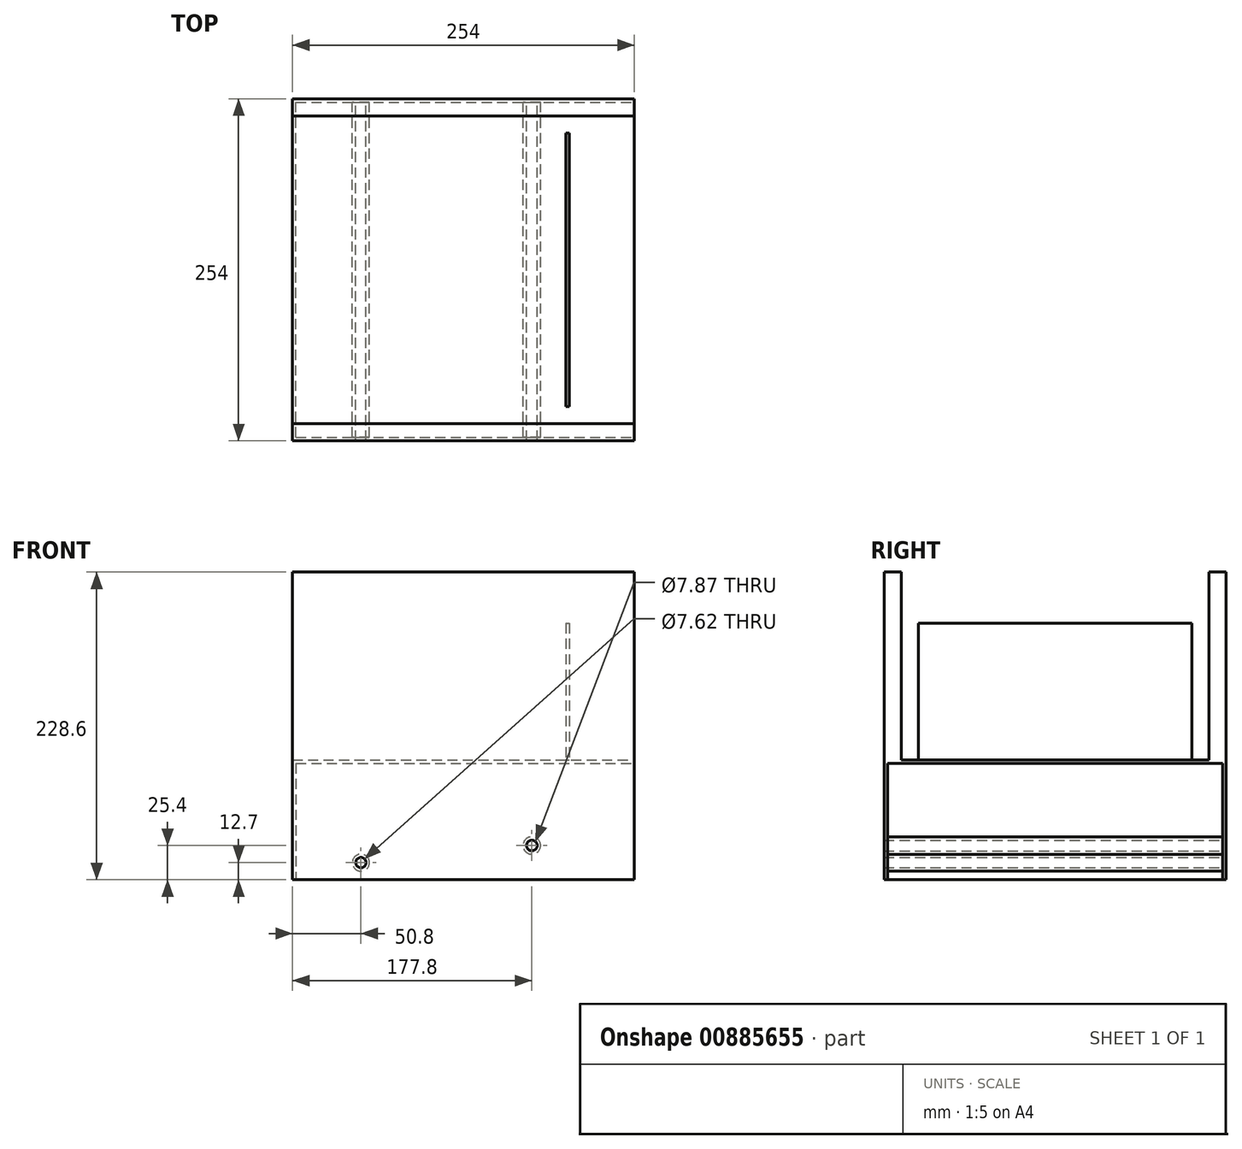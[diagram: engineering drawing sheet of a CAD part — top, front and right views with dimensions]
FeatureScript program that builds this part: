
annotation { "Feature Type Name" : "Feature", "Feature Type Description" : "" }
export const myFeature = defineFeature(function(context is Context, id is Id, definition is map)
    precondition{}
    {
        {
            var Q0;
            Q0=qCreatedBy(makeId("Front.planeOp"),FACE);
            var sketch = newSketch(context, id + "F0", { "sketchPlane" : qUnion([Q0])});
            skLineSegment(sketch, "E0.bottom", {"start": v(-152.4, 0) * mm, "end": v(101.6, 0) * mm});
            skLineSegment(sketch, "E0.top", {"start": v(-152.4, -88.9) * mm, "end": v(101.6, -88.9) * mm});
            skLineSegment(sketch, "E0.left", {"start": v(-152.4, 0) * mm, "end": v(-152.4, -88.9) * mm});
            skLineSegment(sketch, "E0.right", {"start": v(101.6, 0) * mm, "end": v(101.6, -88.9) * mm});
            skCircle(sketch, "E1", {"center": v(25.4, -63.5) * mm, "radius": 3.94 * mm});
            skCircle(sketch, "E2", {"center": v(-101.6, -76.2) * mm, "radius": 3.81 * mm});
            skSolve(sketch);
        }
        {
            var Q0;
            Q0 = qSketchRegion(id + "F0", true);
            extrude(context, id + "F1", {"entities" : qUnion([Q0]), "depth" : 127 * mm, "offsetDistance" : 25.4 * mm});
        }
        {
            var Q0;
            Q0=makeQuery(id+"F1.opExtrude","CAP_FACE",FACE,{"disambiguationData":[OSD([sQuery(id+"F0.wireOp",EDGE,"E0.bottom"),sQuery(id+"F0.wireOp",EDGE,"E0.top"),sQuery(id+"F0.wireOp",EDGE,"E0.left"),sQuery(id+"F0.wireOp",EDGE,"E0.right")])],"isStart":true});
            var Q1;
            Q1=makeQuery(id+"F1.opExtrude","SWEPT_FACE",FACE,{"disambiguationData":[OSD([sQuery(id+"F0.wireOp",EDGE,"E0.top")])]});
            var Q2;
            Q2=makeQuery(id+"F1.opExtrude","SWEPT_FACE",FACE,{"disambiguationData":[OSD([sQuery(id+"F0.wireOp",EDGE,"E0.right")])]});
            shell(context, id + "F2", {"entities" : qUnion([Q0, Q1, Q2]), "thickness" : 2.54 * mm});
        }
        {
            var Q0;
            Q0=makeQuery(id+"F1.opExtrude","SWEPT_FACE",FACE,{"disambiguationData":[OSD([sQuery(id+"F0.wireOp",EDGE,"E0.bottom")])]});
            var sketch = newSketch(context, id + "F3", { "sketchPlane" : qUnion([Q0])});
            skLineSegment(sketch, "E3.bottom", {"start": v(50.8, 0) * mm, "end": v(53.34, 0) * mm});
            skLineSegment(sketch, "E3.top", {"start": v(50.8, -101.6) * mm, "end": v(53.34, -101.6) * mm});
            skLineSegment(sketch, "E3.left", {"start": v(50.8, 0) * mm, "end": v(50.8, -101.6) * mm});
            skLineSegment(sketch, "E3.right", {"start": v(53.34, 0) * mm, "end": v(53.34, -101.6) * mm});
            skSolve(sketch);
        }
        {
            var Q0;
            Q0 = qSketchRegion(id + "F3", true);
            extrude(context, id + "F4", {"entities" : qUnion([Q0]), "operationType" : NewBodyOperationType.ADD, "depth" : 101.6 * mm, "offsetDistance" : 25.4 * mm});
        }
        {
            var Q0;
            {var subQ0=makeQuery(id+"F1.opExtrude","SWEPT_FACE",FACE,{"disambiguationData":[OSD([sQuery(id+"F0.wireOp",EDGE,"E0.bottom")])]});Q0=makeQuery(id+"F7.boolean.opBoolean","MERGE",FACE,{"derivedFrom":[subQ0,makeQuery(id+"F7.opPattern","COPY",FACE,{"derivedFrom":subQ0,"instanceName":"1"})]});}
            var sketch = newSketch(context, id + "F5", { "sketchPlane" : qUnion([Q0])});
            skLineSegment(sketch, "E4.bottom", {"start": v(-152.4, -114.3) * mm, "end": v(101.6, -114.3) * mm});
            skLineSegment(sketch, "E4.top", {"start": v(-152.4, -127) * mm, "end": v(101.6, -127) * mm});
            skLineSegment(sketch, "E4.left", {"start": v(-152.4, -114.3) * mm, "end": v(-152.4, -127) * mm});
            skLineSegment(sketch, "E4.right", {"start": v(101.6, -114.3) * mm, "end": v(101.6, -127) * mm});
            skSolve(sketch);
        }
        {
            var Q0;
            Q0=makeQuery(id+"F5.imprint","IMPRINT",FACE,{"disambiguationData":[TD([[makeQuery(id+"F5.imprint","IMPRINT",EDGE,{"derivedFrom":sQuery(id+"F5.wireOp",EDGE,"E4.bottom")}),-1.0]])]});
            extrude(context, id + "F6", {"entities" : qUnion([Q0]), "operationType" : NewBodyOperationType.ADD, "depth" : 139.7 * mm, "offsetDistance" : 25.4 * mm});
        }
        {
            var Q0;
            Q0=makeQuery(id+"F1.opExtrude","SWEPT_BODY",BODY,{"disambiguationData":[OSD([sQuery(id+"F0.wireOp",EDGE,"E0.bottom"),sQuery(id+"F0.wireOp",EDGE,"E0.top"),sQuery(id+"F0.wireOp",EDGE,"E0.left"),sQuery(id+"F0.wireOp",EDGE,"E0.right")])]});
            var Q1;
            Q1=qCreatedBy(makeId("Front.planeOp"),FACE);
            mirror(context, id + "F7", {"operationType" : NewBodyOperationType.ADD, "entities" : qUnion([Q0]), "mirrorPlane" : qUnion([Q1])});
        }
    });
